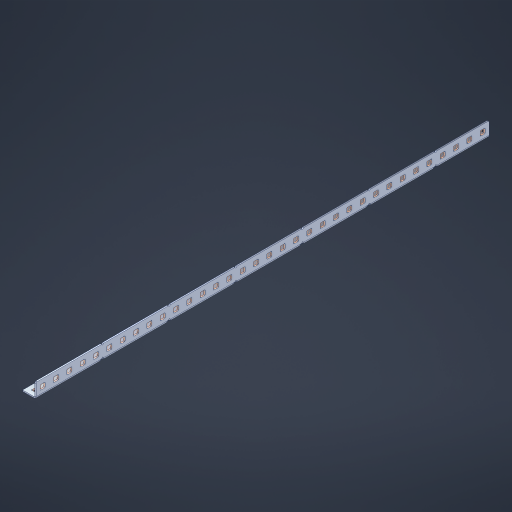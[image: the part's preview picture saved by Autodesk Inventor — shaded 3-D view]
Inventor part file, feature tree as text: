
AUTODESK INVENTOR PART (.ipt)
format: ipt  version: 2023 (Build 270158000, 158)  size: 1,025,024 bytes
history: native  units: in
note: dims shown in document units (in); Inventor stores cm internally (conversion verified against a paired STEP export)
features: other x73, extrude x67, sheet_metal_op x10, sketch x8, mirror x1, pattern_linear x1, chamfer x1
ambient origin geometry x8: Origin, YZ Plane, XZ Plane, XY Plane, X Axis, Y Axis, Z Axis, Center Point
bodies: Solid1 (feature_tree), Body (feature_tree)
feature tree (161):
  other  "Flange Pattern Plane"
  sheet_metal_op  "Flange Pattern"
  sheet_metal_op  "Body Pattern"
  other  "Arc Length"
  mirror  "Notch Mirror"
  pattern_linear  "Notch Pattern"  Spacing1=0.1875in  [1 undecoded]
  chamfer  "End Chamfer"
  extrude  "Half Cut"  Depth=0.0469in
  sketch  "Sketch1"  dims[d0=2.5in]
  other  "Plate1"
  sketch  "Sketch2"  dims[d1=17.0in]
  other  "Plate2"
  sheet_metal_op  "Bend1"
  sheet_metal_op  "Corner1"
  sketch  "Sketch3"  dims[d2=0.0469in]
  other  "Flange Pattern Sketch"
  sketch  "Sketch7"  dims[d3=0.0469in]
  other  "Srf1"
  other  "Srf2"
  sketch  "Sketch8"  dims[d4=0.0234in]
  sketch  "Sketch9"  dims[d5=0.0938in]
  other  "Srf91"
  sheet_metal_op  "Body Pattern Sketch"
  other  "Srf92"
  sketch  "Sketch13"  dims[d6=0.0469in]
  sketch  "Sketch14"  dims[d7=0.5in d8=90.0deg d9=0.0312in d10=0.1875in d11=0.0469in d12=0.0469in d16=0.182in d17=0.02in d18=0.0469in d19=0.0in d20=0.25in d21=0.25in d46=0.172in d47=1.0in d48=0.0in d49=0.182in d50=0.02in d51=0.25in d52=0.25in d53=0.0469in d54=0.0in d55=0.172in d56=1.0in d57=0.0in d60=13.3858in d62=0.5in d63=0.3937in d65=0.5in d85=0.1227in d86=0.1659in d88=0.04in d89=0.0469in d90=0.0in d91=0.04in d92=0.0491in d95=2.5in d96=0.04in d97=0.25in d98=45.0deg d101=0.0in d102=2.497in d131=0.5in d132=13.3858in d134=0.5in d139=0.5in]
  other  "Srf856"
  other  "Srf1310"
  other  "Srf1311"
  other  "Srf1312"
  other  "Srf1376"
  other  "Srf1377"
  other  "Srf1728"
  other  "Srf1755"
  other  "Srf1878"
  other  "Srf1879"
  other  "Srf1880"
  other  "Srf1881"
  other  "Srf1882"
  other  "Srf1883"
  other  "Srf1884"
  other  "Srf1885"
  other  "Srf1886"
  other  "Srf1887"
  other  "Srf1888"
  other  "Srf1889"
  other  "Srf1890"
  other  "Srf1891"
  other  "Srf1892"
  other  "Srf1893"
  other  "Srf1894"
  other  "Srf1895"
  other  "Srf1896"
  other  "Srf1897"
  other  "Srf1898"
  other  "Srf1899"
  other  "Srf1900"
  other  "Srf1901"
  other  "Srf1902"
  other  "Srf1903"
  other  "Srf1904"
  other  "Srf1905"
  other  "Srf1942"
  other  "Srf1943"
  other  "Srf1944"
  other  "Srf1945"
  other  "Srf1946"
  other  "Srf1947"
  other  "Srf1948"
  other  "Srf1949"
  other  "Srf1950"
  other  "Srf1951"
  other  "Srf1952"
  other  "Srf1953"
  other  "Srf1954"
  other  "Srf1955"
  other  "Srf1956"
  other  "Srf1957"
  other  "Srf1958"
  other  "Srf1959"
  other  "Srf1960"
  other  "Srf1961"
  other  "Srf1962"
  other  "Srf1963"
  other  "Srf1964"
  other  "Srf1965"
  other  "Srf1966"
  other  "Srf1967"
  other  "Srf1968"
  other  "Srf1969"
  sheet_metal_op  "Flange Stamp"
  sheet_metal_op  "Flange Circle"
  sheet_metal_op  "Body Stamp"
  sheet_metal_op  "Body Circle"
  sheet_metal_op  "Notch"
  extrude  "ExtrusionSrf2"  Depth=0.0469in
  extrude  "ExtrusionSrf92"  Depth=0.5in
  extrude  "ExtrusionSrf856"  Depth=0.02in
  extrude  "ExtrusionSrf1310"  Depth=0.0469in
  extrude  "ExtrusionSrf1311"  TaperAngle=0.0deg  [1 undecoded]
  extrude  "ExtrusionSrf1312"  Depth=0.5in
  extrude  "ExtrusionSrf1376"  Depth=0.5in
  extrude  "ExtrusionSrf1377"  Depth=0.5in
  extrude  "ExtrusionSrf1728"  Depth=0.5in TaperAngle=0.0deg
  extrude  "ExtrusionSrf1755"  Depth=0.5in
  extrude  "ExtrusionSrf1878"  Depth=0.02in
  extrude  "ExtrusionSrf1879"  Depth=0.5in
  extrude  "ExtrusionSrf1880"  Depth=0.5in
  extrude  "ExtrusionSrf1881"  Depth=0.0469in
  extrude  "ExtrusionSrf1882"  TaperAngle=0.0deg  [1 undecoded]
  extrude  "ExtrusionSrf1883"  Depth=0.5in
  extrude  "ExtrusionSrf1884"  Depth=0.5in TaperAngle=0.0deg
  extrude  "ExtrusionSrf1885"  Depth=0.5in
  extrude  "ExtrusionSrf1886"  Depth=0.5in
  extrude  "ExtrusionSrf1887"  Depth=0.5in
  extrude  "ExtrusionSrf1888"  Depth=0.5in
  extrude  "ExtrusionSrf1889"  Depth=0.5in
  extrude  "ExtrusionSrf1890"  Depth=0.0469in
  extrude  "ExtrusionSrf1891"  TaperAngle=0.0deg  [1 undecoded]
  extrude  "ExtrusionSrf1892"  Depth=0.5in
  extrude  "ExtrusionSrf1893"  Depth=0.5in
  extrude  "ExtrusionSrf1894"  Depth=0.5in
  extrude  "ExtrusionSrf1895"  Depth=0.5in TaperAngle=45.0deg
  extrude  "ExtrusionSrf1896"  TaperAngle=0.0deg  [1 undecoded]
  extrude  "ExtrusionSrf1897"  Depth=0.5in
  extrude  "ExtrusionSrf1898"  Depth=0.5in
  extrude  "ExtrusionSrf1899"  Depth=0.5in
  extrude  "ExtrusionSrf1900"  Depth=0.5in
  extrude  "ExtrusionSrf1901"  Depth=0.5in
  extrude  "ExtrusionSrf1902"  [1 undecoded]
  extrude  "ExtrusionSrf1903"  [1 undecoded]
  extrude  "ExtrusionSrf1904"  [1 undecoded]
  extrude  "ExtrusionSrf1905"  [1 undecoded]
  extrude  "ExtrusionSrf1942"  [1 undecoded]
  extrude  "ExtrusionSrf1943"  [1 undecoded]
  extrude  "ExtrusionSrf1944"  [1 undecoded]
  extrude  "ExtrusionSrf1945"  [1 undecoded]
  extrude  "ExtrusionSrf1946"  [1 undecoded]
  extrude  "ExtrusionSrf1947"  [1 undecoded]
  extrude  "ExtrusionSrf1948"  [1 undecoded]
  extrude  "ExtrusionSrf1949"  [1 undecoded]
  extrude  "ExtrusionSrf1950"  [1 undecoded]
  extrude  "ExtrusionSrf1951"  [1 undecoded]
  extrude  "ExtrusionSrf1952"  [1 undecoded]
  extrude  "ExtrusionSrf1953"  [1 undecoded]
  extrude  "ExtrusionSrf1954"  [1 undecoded]
  extrude  "ExtrusionSrf1955"  [1 undecoded]
  extrude  "ExtrusionSrf1956"  [1 undecoded]
  extrude  "ExtrusionSrf1957"  [1 undecoded]
  extrude  "ExtrusionSrf1958"  [1 undecoded]
  extrude  "ExtrusionSrf1959"  [1 undecoded]
  extrude  "ExtrusionSrf1960"  [1 undecoded]
  extrude  "ExtrusionSrf1961"  [1 undecoded]
  extrude  "ExtrusionSrf1962"  [1 undecoded]
  extrude  "ExtrusionSrf1963"  [1 undecoded]
  extrude  "ExtrusionSrf1964"  [1 undecoded]
  extrude  "ExtrusionSrf1965"  [1 undecoded]
  extrude  "ExtrusionSrf1966"  [1 undecoded]
  extrude  "ExtrusionSrf1967"  [1 undecoded]
  extrude  "ExtrusionSrf1968"  [1 undecoded]
  extrude  "ExtrusionSrf1969"  [1 undecoded]
note: 37 required parameter values undecoded (feature->parameter linkage not recoverable at this tier; creation-order binding heuristic only, values carry confidence <= 0.55)
